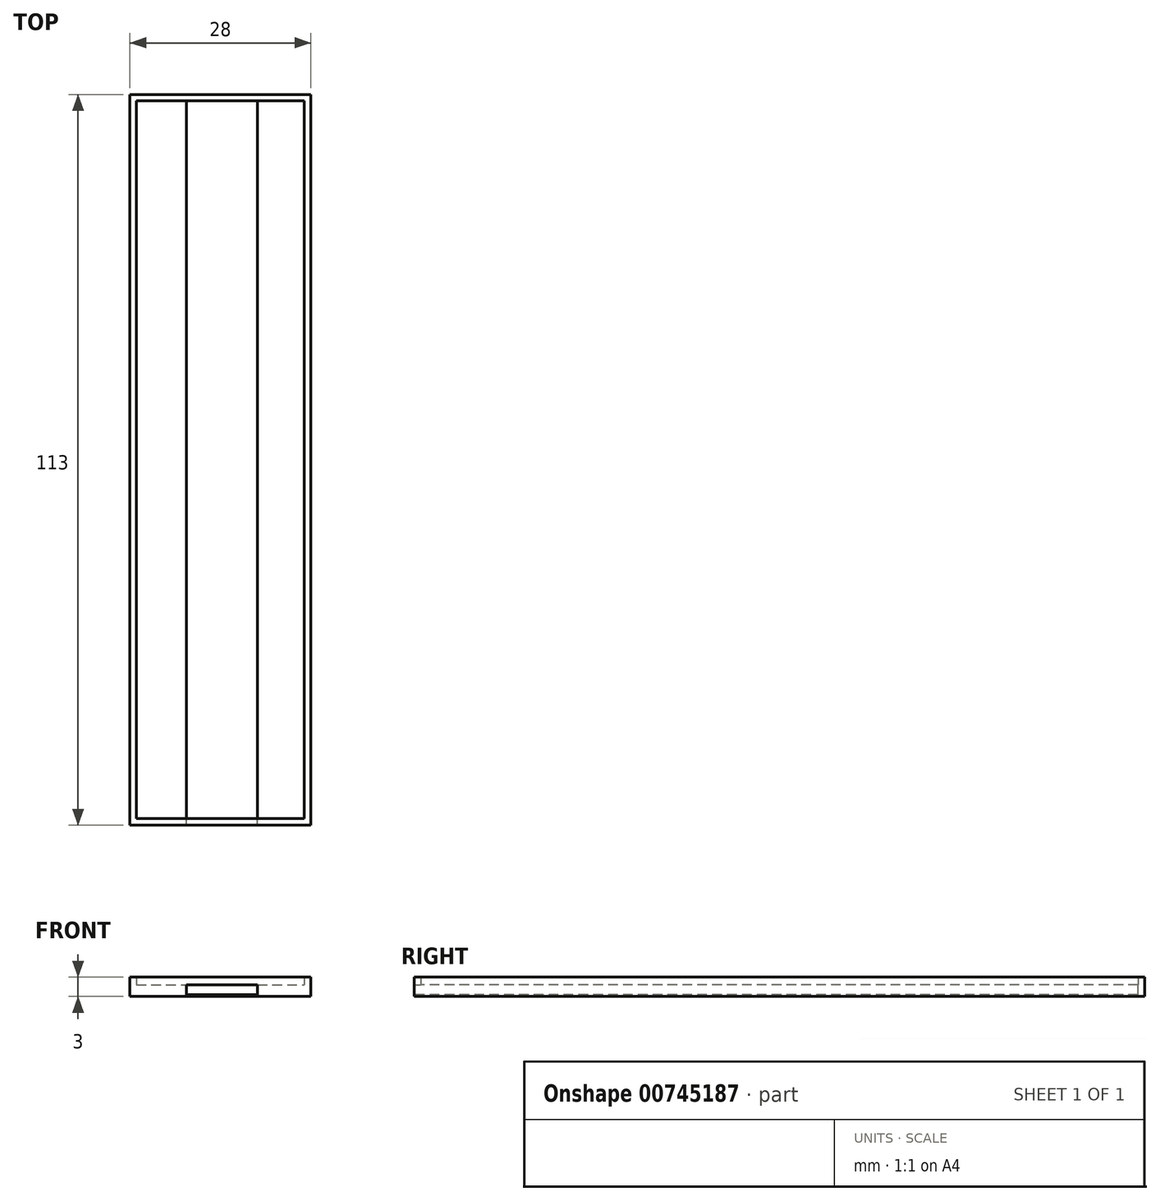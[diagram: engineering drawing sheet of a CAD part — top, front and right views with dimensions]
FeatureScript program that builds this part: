
annotation { "Feature Type Name" : "Feature", "Feature Type Description" : "" }
export const myFeature = defineFeature(function(context is Context, id is Id, definition is map)
    precondition{}
    {
        {
            var Q0;
            Q0=qCreatedBy(makeId("Top.planeOp"),FACE);
            var sketch = newSketch(context, id + "F0", { "sketchPlane" : qUnion([Q0])});
            skLineSegment(sketch, "E0.bottom", {"start": v(-30, 55.02) * mm, "end": v(-4, 55.02) * mm});
            skLineSegment(sketch, "E0.top", {"start": v(-30, -55.98) * mm, "end": v(-4, -55.98) * mm});
            skLineSegment(sketch, "E0.left", {"start": v(-30, 55.02) * mm, "end": v(-30, -55.98) * mm});
            skLineSegment(sketch, "E0.right", {"start": v(-4, 55.02) * mm, "end": v(-4, -55.98) * mm});
            skSolve(sketch);
        }
        {
            var Q0;
            Q0=makeQuery(id+"F0.imprint","IMPRINT",FACE,{"disambiguationData":[TD([[makeQuery(id+"F0.imprint","IMPRINT",EDGE,{"derivedFrom":sQuery(id+"F0.wireOp",EDGE,"E0.bottom")}),-1.0]])]});
            extrude(context, id + "F1", {"entities" : qUnion([Q0]), "depth" : 1 * mm, "offsetDistance" : 25 * mm});
        }
        {
            var Q0;
            Q0=makeQuery(id+"F1.opExtrude","CAP_FACE",FACE,{"disambiguationData":[OSD([sQuery(id+"F0.wireOp",EDGE,"E0.bottom"),sQuery(id+"F0.wireOp",EDGE,"E0.top"),sQuery(id+"F0.wireOp",EDGE,"E0.left"),sQuery(id+"F0.wireOp",EDGE,"E0.right")])],"isStart":false});
            shell(context, id + "F2", {"entities" : qUnion([Q0]), "thickness" : 1 * mm, "oppositeDirection" : true});
        }
        {
            var Q0;
            Q0=makeQuery(id+"F2.opShell","OFFSET_FACE",FACE,{"disambiguationData":[OSD([sQuery(id+"F0.wireOp",EDGE,"E0.bottom"),sQuery(id+"F0.wireOp",EDGE,"E0.top"),sQuery(id+"F0.wireOp",EDGE,"E0.left"),sQuery(id+"F0.wireOp",EDGE,"E0.right")])]});
            extrude(context, id + "F3", {"entities" : qUnion([Q0]), "operationType" : NewBodyOperationType.ADD, "depth" : .8 * mm, "offsetDistance" : 25 * mm});
        }
        {
            var Q0;
            Q0=makeQuery(id+"F3.opExtrude","CAP_FACE",FACE,{"disambiguationData":[OSD([sQuery(id+"F0.wireOp",EDGE,"E0.bottom"),sQuery(id+"F0.wireOp",EDGE,"E0.top"),sQuery(id+"F0.wireOp",EDGE,"E0.left"),sQuery(id+"F0.wireOp",EDGE,"E0.right")])],"isStart":false});
            var sketch = newSketch(context, id + "F4", { "sketchPlane" : qUnion([Q0])});
            skLineSegment(sketch, "E1.bottom", {"start": v(-22.25, 55.02) * mm, "end": v(-11.25, 55.02) * mm});
            skLineSegment(sketch, "E1.top", {"start": v(-22.25, -55.98) * mm, "end": v(-11.25, -55.98) * mm});
            skLineSegment(sketch, "E1.left", {"start": v(-22.25, 55.02) * mm, "end": v(-22.25, -55.98) * mm});
            skLineSegment(sketch, "E1.right", {"start": v(-11.25, 55.02) * mm, "end": v(-11.25, -55.98) * mm});
            skSolve(sketch);
        }
        {
            var Q0;
            {var subQ0=sQuery(id+"F4.wireOp",EDGE,"E1.left");var subQ1=sQuery(id+"F0.wireOp",EDGE,"E0.bottom");var subQ2=makeQuery(id+"F2.opShell","OFFSET_EDGE",EDGE,{"disambiguationData":[OSD([subQ1]),TDD([makeQuery(id+"F1.opExtrude","CAP_EDGE",EDGE,{"disambiguationData":[OSD([subQ1])],"isStart":true})])]});var subQ3=makeQuery(id+"F4.imprint","INTERSECT",VERTEX,{"derivedFrom":[subQ2,subQ0]});Q0=makeQuery(id+"F4.imprint","IMPRINT",FACE,{"disambiguationData":[TD([[makeQuery(id+"F4.imprint","IMPRINT",EDGE,{"disambiguationData":[TD([[subQ3,-1.0]])],"derivedFrom":subQ0}),1.0]])]});}
            extrude(context, id + "F5", {"entities" : qUnion([Q0]), "operationType" : NewBodyOperationType.REMOVE, "oppositeDirection" : true, "depth" : 1.5 * mm, "offsetDistance" : 25 * mm});
        }
        {
            var Q0;
            Q0=makeQuery(id+"F1.opExtrude","CAP_FACE",FACE,{"disambiguationData":[OSD([sQuery(id+"F0.wireOp",EDGE,"E0.bottom"),sQuery(id+"F0.wireOp",EDGE,"E0.top"),sQuery(id+"F0.wireOp",EDGE,"E0.left"),sQuery(id+"F0.wireOp",EDGE,"E0.right")])],"isStart":false});
            extrude(context, id + "F6", {"entities" : qUnion([Q0]), "operationType" : NewBodyOperationType.ADD, "depth" : 1 * mm, "offsetDistance" : 25 * mm});
        }
        {
            var Q0;
            {var subQ0=sQuery(id+"F0.wireOp",EDGE,"E0.top");Q0=makeQuery(id+"F6.boolean.opBoolean","MERGE",FACE,{"derivedFrom":[makeQuery(id+"F5.boolean.opBoolean","MERGE",FACE,{"derivedFrom":[makeQuery(id+"F2.opShell","OFFSET_FACE",FACE,{"disambiguationData":[OSD([subQ0])]}),makeQuery(id+"F5.opExtrude","SWEPT_FACE",FACE,{"disambiguationData":[OSD([sQuery(id+"F4.wireOp",EDGE,"E1.top")])]})]}),makeQuery(id+"F6.opExtrude","SWEPT_FACE",FACE,{"disambiguationData":[OSD([subQ0]),TDD([makeQuery(id+"F2.opShell","OFFSET_EDGE",EDGE,{"disambiguationData":[OSD([subQ0]),TDD([makeQuery(id+"F1.opExtrude","CAP_EDGE",EDGE,{"disambiguationData":[OSD([subQ0])],"isStart":false})])]})])]})]});}
            var sketch = newSketch(context, id + "F7", { "sketchPlane" : qUnion([Q0])});
            skLineSegment(sketch, "E2", {"start": v(11.25, 0.8) * mm, "end": v(22.25, 0.8) * mm});
            skSolve(sketch);
        }
        {
            var Q0;
            Q0=makeQuery(id+"F7.imprint","IMPRINT",FACE,{"disambiguationData":[TD([[makeQuery(id+"F7.imprint","IMPRINT",EDGE,{"derivedFrom":sQuery(id+"F7.wireOp",EDGE,"E2")}),-1.0]])]});
            extrude(context, id + "F8", {"entities" : qUnion([Q0]), "operationType" : NewBodyOperationType.REMOVE, "endBound" : BoundingType.UP_TO_NEXT, "oppositeDirection" : true, "depth" : 25 * mm, "offsetDistance" : 25 * mm});
        }
    });
